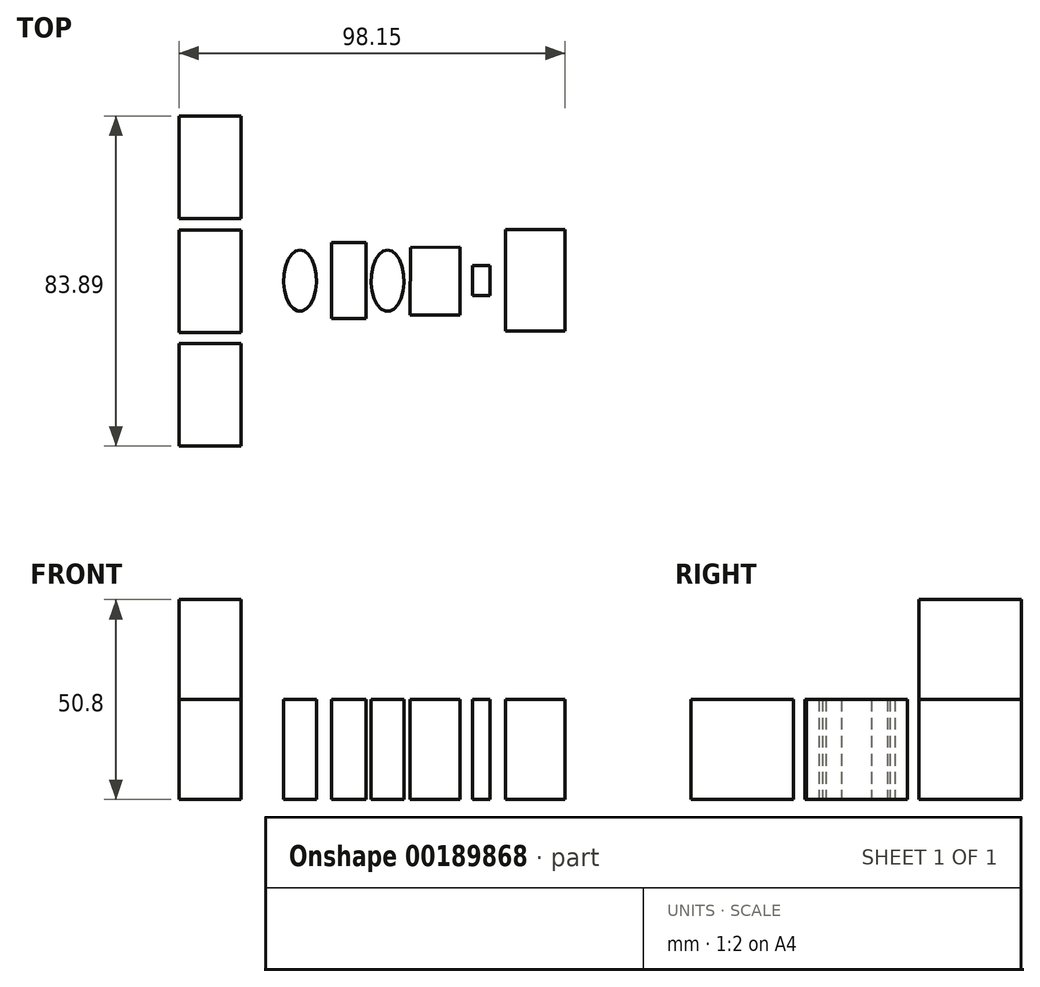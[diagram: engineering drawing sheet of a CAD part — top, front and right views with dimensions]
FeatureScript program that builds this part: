
annotation { "Feature Type Name" : "Feature", "Feature Type Description" : "" }
export const myFeature = defineFeature(function(context is Context, id is Id, definition is map)
    precondition{}
    {
        {
            var Q0;
            Q0=qCreatedBy(makeId("Top.planeOp"),FACE);
            var sketch = newSketch(context, id + "F0", { "sketchPlane" : qUnion([Q0])});
            skLineSegment(sketch, "E0.bottom", {"start": v(-82.35, 26.16) * mm, "end": v(-98.15, 26.16) * mm});
            skLineSegment(sketch, "E0.top", {"start": v(-82.35, 52.2) * mm, "end": v(-98.15, 52.2) * mm});
            skLineSegment(sketch, "E0.left", {"start": v(-82.35, 26.16) * mm, "end": v(-82.35, 52.2) * mm});
            skLineSegment(sketch, "E0.right", {"start": v(-98.15, 26.16) * mm, "end": v(-98.15, 52.2) * mm});
            skPoint(sketch, "E0.middle", {"position": v(-90.25, 39.18) * mm});
            skLineSegment(sketch, "E1.bottom", {"start": v(-82.35, -2.76) * mm, "end": v(-98.15, -2.76) * mm});
            skLineSegment(sketch, "E1.top", {"start": v(-82.35, 23.27) * mm, "end": v(-98.15, 23.27) * mm});
            skLineSegment(sketch, "E1.left", {"start": v(-82.35, -2.76) * mm, "end": v(-82.35, 23.27) * mm});
            skLineSegment(sketch, "E1.right", {"start": v(-98.15, -2.76) * mm, "end": v(-98.15, 23.27) * mm});
            skPoint(sketch, "E1.middle", {"position": v(-90.25, 10.25) * mm});
            skLineSegment(sketch, "E2.bottom", {"start": v(-82.38, -31.7) * mm, "end": v(-98.13, -31.7) * mm});
            skLineSegment(sketch, "E2.top", {"start": v(-82.38, -5.66) * mm, "end": v(-98.13, -5.66) * mm});
            skLineSegment(sketch, "E2.left", {"start": v(-82.38, -31.7) * mm, "end": v(-82.38, -5.66) * mm});
            skLineSegment(sketch, "E2.right", {"start": v(-98.13, -31.7) * mm, "end": v(-98.13, -5.66) * mm});
            skPoint(sketch, "E2.middle", {"position": v(-90.25, -18.67) * mm});
            skLineSegment(sketch, "E3", {"start": v(-82.35, 39.18) * mm, "end": v(-75.37, 39.18) * mm});
            skLineSegment(sketch, "E4", {"start": v(-75.37, 39.18) * mm, "end": v(-75.37, 10.39) * mm});
            skLineSegment(sketch, "E5", {"start": v(-75.37, 10.39) * mm, "end": v(-75.37, -19.12) * mm});
            skLineSegment(sketch, "E6", {"start": v(-75.37, -19.12) * mm, "end": v(-82.35, -19.12) * mm});
            skLineSegment(sketch, "E7", {"start": v(-75.37, 10.39) * mm, "end": v(-59.38, 10.39) * mm});
            skLineSegment(sketch, "E8", {"start": v(-75.37, 10.39) * mm, "end": v(-82.35, 10.39) * mm});
            skLineSegment(sketch, "E9.bottom", {"start": v(-59.38, 20.06) * mm, "end": v(-50.54, 20.06) * mm});
            skLineSegment(sketch, "E9.top", {"start": v(-59.38, 0.72) * mm, "end": v(-50.54, 0.72) * mm});
            skLineSegment(sketch, "E9.left", {"start": v(-59.38, 20.06) * mm, "end": v(-59.38, 0.72) * mm});
            skLineSegment(sketch, "E9.right", {"start": v(-50.54, 20.06) * mm, "end": v(-50.54, 0.72) * mm});
            skEllipse(sketch, "E10", {"center": v(-45.13, 10.34) * mm, "majorRadius": 7.79 * mm, "minorRadius": 4.2 * mm, "majorAxis": v(0, 1)});
            skEllipse(sketch, "E11", {"center": v(-67.38, 10.39) * mm, "majorRadius": 7.79 * mm, "minorRadius": 4.2 * mm, "majorAxis": v(0, 1)});
            skLineSegment(sketch, "E12", {"start": v(-50.54, 10.39) * mm, "end": v(-49.32, 10.39) * mm});
            skLineSegment(sketch, "E13.bottom", {"start": v(-26.69, 18.83) * mm, "end": v(-39.25, 18.78) * mm});
            skLineSegment(sketch, "E13.top", {"start": v(-26.69, 1.65) * mm, "end": v(-39.44, 1.65) * mm});
            skLineSegment(sketch, "E13.right", {"start": v(-26.69, 18.83) * mm, "end": v(-26.69, 1.65) * mm});
            skLineSegment(sketch, "E14", {"start": v(-40.94, 10.34) * mm, "end": v(-39.5, 10.34) * mm});
            skLineSegment(sketch, "E15", {"start": v(-39.44, 1.65) * mm, "end": v(-26.69, 18.83) * mm});
            skLineSegment(sketch, "E16", {"start": v(-26.69, 10.24) * mm, "end": v(-23.49, 10.24) * mm});
            skLineSegment(sketch, "E17", {"start": v(-40.94, 10.34) * mm, "end": v(-49.32, 10.39) * mm});
            skLineSegment(sketch, "E18", {"start": v(-39.25, 18.78) * mm, "end": v(-39.44, 1.65) * mm});
            skLineSegment(sketch, "E19.bottom", {"start": v(-23.6, 14.18) * mm, "end": v(-23.49, 14.18) * mm});
            skLineSegment(sketch, "E19.top", {"start": v(-23.6, 6.52) * mm, "end": v(-23.49, 6.52) * mm});
            skLineSegment(sketch, "E19.left", {"start": v(-23.6, 14.18) * mm, "end": v(-23.6, 6.52) * mm});
            skLineSegment(sketch, "E19.right", {"start": v(-23.49, 14.18) * mm, "end": v(-23.49, 6.52) * mm});
            skLineSegment(sketch, "E20.bottom", {"start": v(-23.49, 6.52) * mm, "end": v(-19.11, 6.52) * mm});
            skLineSegment(sketch, "E20.top", {"start": v(-23.49, 6.52) * mm, "end": v(-19.11, 6.52) * mm});
            skLineSegment(sketch, "E20.left", {"start": v(-23.49, 6.52) * mm, "end": v(-23.49, 6.52) * mm});
            skLineSegment(sketch, "E20.right", {"start": v(-19.11, 6.52) * mm, "end": v(-19.11, 6.52) * mm});
            skLineSegment(sketch, "E21", {"start": v(-19.11, 6.52) * mm, "end": v(-19.11, 14.18) * mm});
            skLineSegment(sketch, "E22", {"start": v(-23.49, 14.18) * mm, "end": v(-19.11, 14.18) * mm});
            skLineSegment(sketch, "E23", {"start": v(-19.11, 10.35) * mm, "end": v(-15.17, 10.35) * mm});
            skLineSegment(sketch, "E24.bottom", {"start": v(-15.17, 23.28) * mm, "end": v(0, 23.28) * mm});
            skLineSegment(sketch, "E24.top", {"start": v(-15.17, -2.44) * mm, "end": v(0, -2.44) * mm});
            skLineSegment(sketch, "E24.left", {"start": v(-15.17, 23.28) * mm, "end": v(-15.17, -2.44) * mm});
            skLineSegment(sketch, "E24.right", {"start": v(0, 23.28) * mm, "end": v(0, -2.44) * mm});
            skSolve(sketch);
        }
        {
            var Q0;
            Q0 = qSketchRegion(id + "F0", true);
            extrude(context, id + "F1", {"entities" : qUnion([Q0]), "depth" : 25.4 * mm});
        }
        {
            var Q0;
            Q0=makeQuery(id+"F1.opExtrude","CAP_FACE",FACE,{"disambiguationData":[OSD([sQuery(id+"F0.wireOp",EDGE,"E0.bottom"),sQuery(id+"F0.wireOp",EDGE,"E0.top"),sQuery(id+"F0.wireOp",EDGE,"E0.left"),sQuery(id+"F0.wireOp",EDGE,"E0.right")])],"isStart":false});
            var Q1;
            Q1 = qSketchRegion(id + "F0", true);
            extrude(context, id + "F2", {"entities" : qUnion([Q0, Q1]), "depth" : 25.4 * mm});
        }
    });
